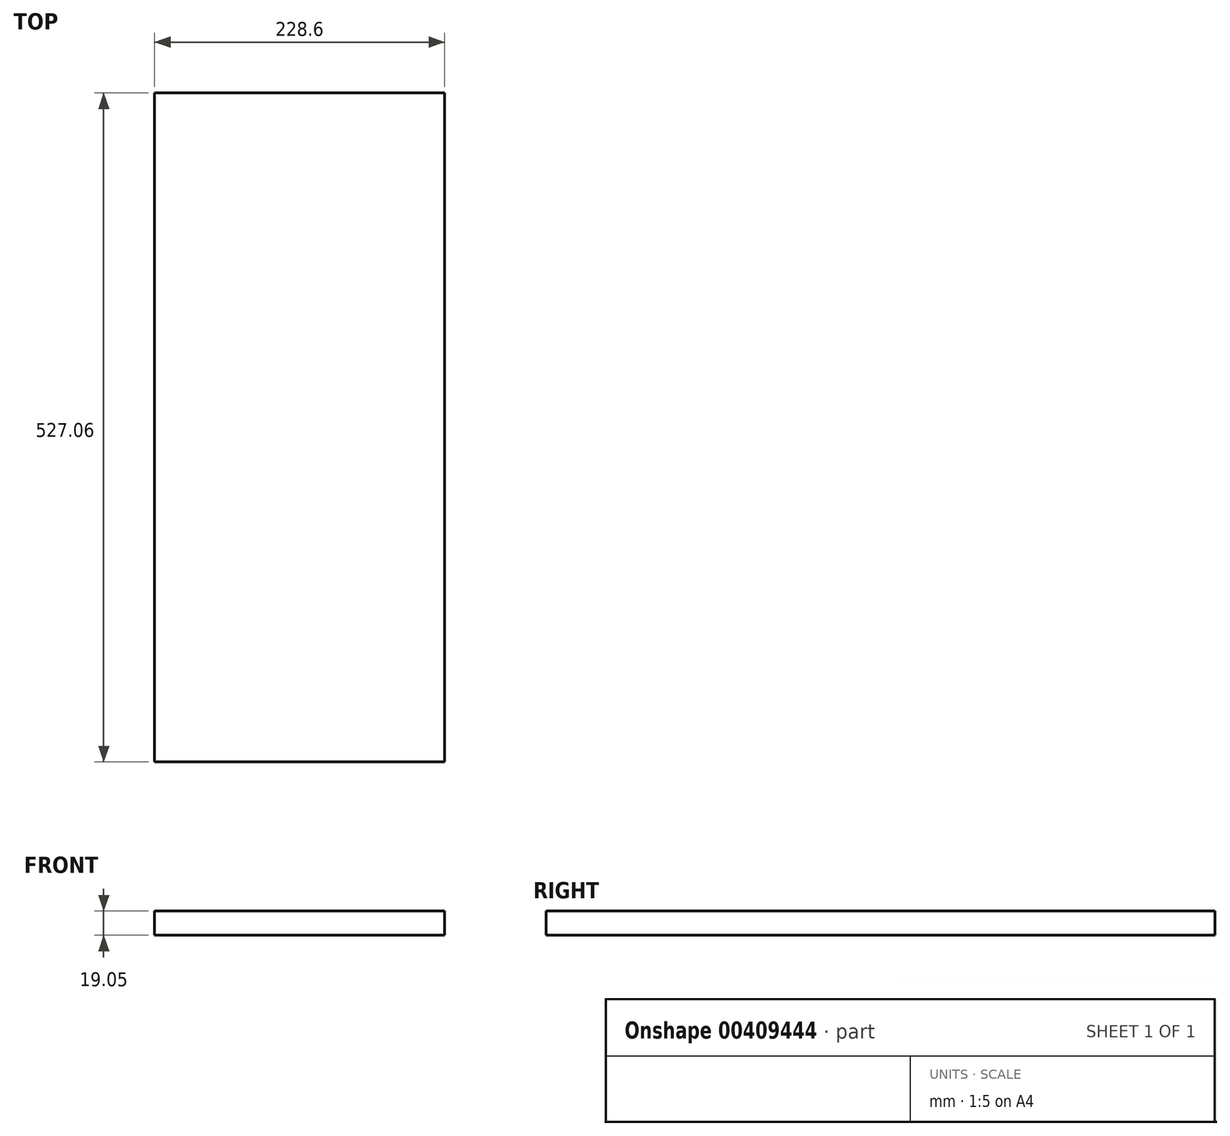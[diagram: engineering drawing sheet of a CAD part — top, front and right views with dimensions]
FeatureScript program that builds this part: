
annotation { "Feature Type Name" : "Feature", "Feature Type Description" : "" }
export const myFeature = defineFeature(function(context is Context, id is Id, definition is map)
    precondition{}
    {
        {
            var Q0;
            Q0=qCreatedBy(makeId("Top.planeOp"),FACE);
            var sketch = newSketch(context, id + "F0", { "sketchPlane" : qUnion([Q0])});
            skLineSegment(sketch, "E0.bottom", {"start": v(114.3, -263.53) * mm, "end": v(-114.3, -263.53) * mm});
            skLineSegment(sketch, "E0.top", {"start": v(114.3, 263.53) * mm, "end": v(-114.3, 263.53) * mm});
            skLineSegment(sketch, "E0.left", {"start": v(114.3, -263.53) * mm, "end": v(114.3, 263.53) * mm});
            skLineSegment(sketch, "E0.right", {"start": v(-114.3, -263.53) * mm, "end": v(-114.3, 263.53) * mm});
            skPoint(sketch, "E0.middle", {"position": v(0, 0) * mm});
            skSolve(sketch);
        }
        {
            var Q0;
            Q0=makeQuery(id+"F0.imprint","IMPRINT",FACE,{"disambiguationData":[TD([[makeQuery(id+"F0.imprint","IMPRINT",EDGE,{"derivedFrom":sQuery(id+"F0.wireOp",EDGE,"E0.bottom")}),-1.0]])]});
            extrude(context, id + "F1", {"entities" : qUnion([Q0]), "depth" : 19.05 * mm});
        }
    });
